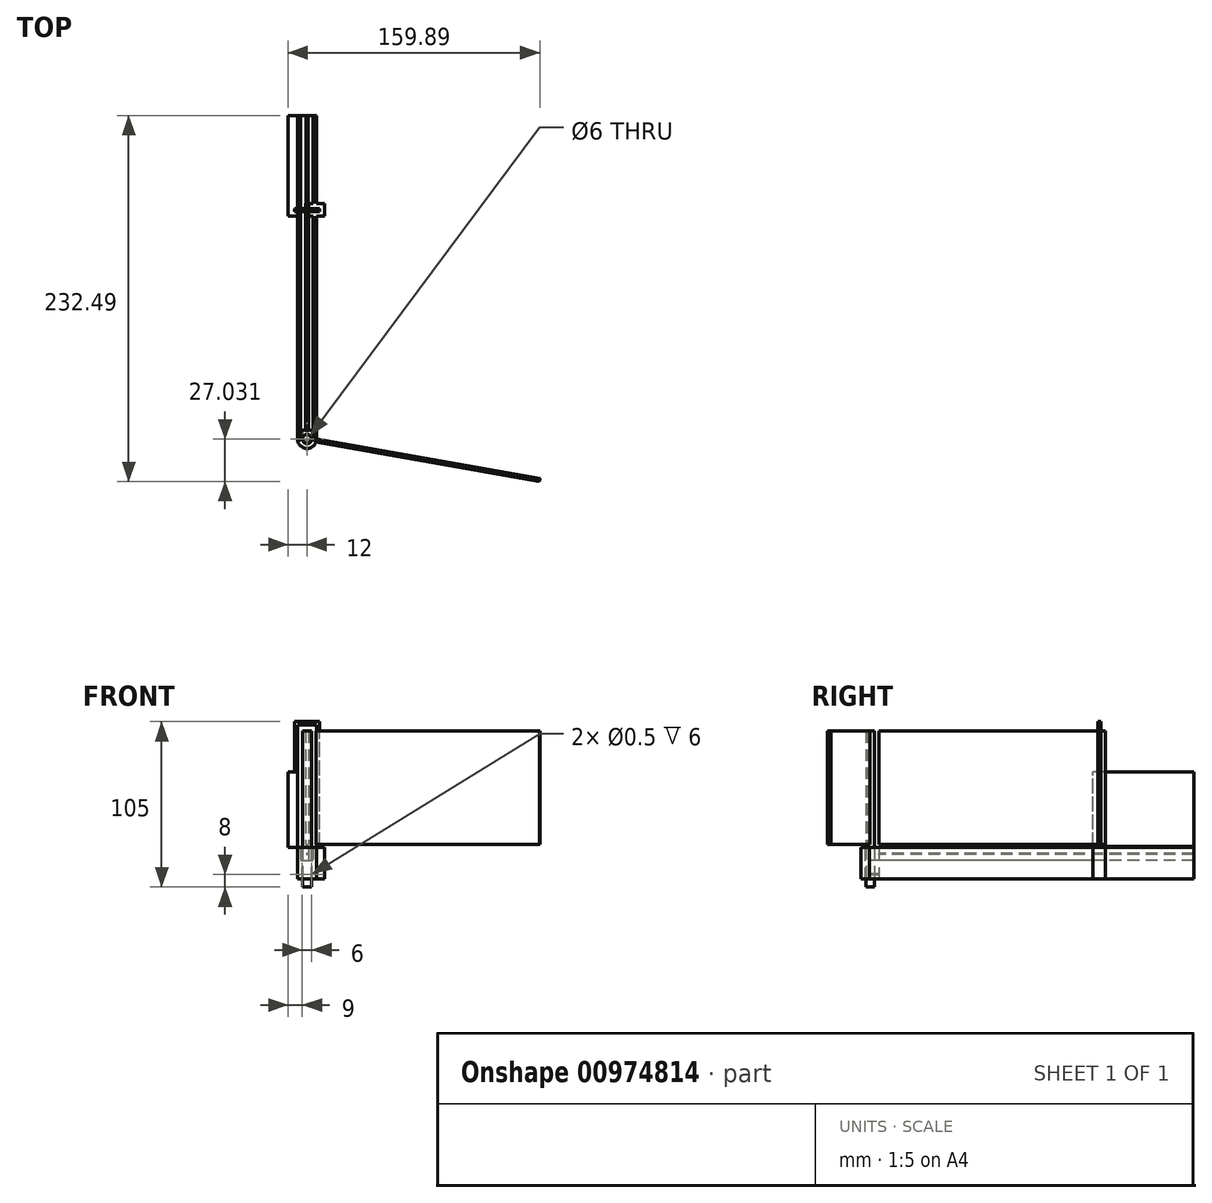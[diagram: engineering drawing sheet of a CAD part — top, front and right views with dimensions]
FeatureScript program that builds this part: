
annotation { "Feature Type Name" : "Feature", "Feature Type Description" : "" }
export const myFeature = defineFeature(function(context is Context, id is Id, definition is map)
    precondition{}
    {
        {
            var Q0;
            Q0=qCreatedBy(makeId("Front.planeOp"),FACE);
            var sketch = newSketch(context, id + "F0", { "sketchPlane" : qUnion([Q0])});
            skLineSegment(sketch, "E0.bottom", {"start": v(2, 0) * mm, "end": v(10, 0) * mm});
            skLineSegment(sketch, "E0.top", {"start": v(2, -8) * mm, "end": v(10, -8) * mm});
            skLineSegment(sketch, "E0.left", {"start": v(2, 0) * mm, "end": v(2, -8) * mm});
            skLineSegment(sketch, "E0.right", {"start": v(10, 0) * mm, "end": v(10, -8) * mm});
            skLineSegment(sketch, "E1.bottom", {"start": v(0, -8) * mm, "end": v(12, -8) * mm});
            skLineSegment(sketch, "E1.top", {"start": v(0, -20) * mm, "end": v(12, -20) * mm});
            skLineSegment(sketch, "E1.left", {"start": v(0, -8) * mm, "end": v(0, -20) * mm});
            skLineSegment(sketch, "E1.right", {"start": v(12, -8) * mm, "end": v(12, -20) * mm});
            skLineSegment(sketch, "E2.bottom", {"start": v(0, 0) * mm, "end": v(2, 0) * mm});
            skLineSegment(sketch, "E2.top", {"start": v(0, -8) * mm, "end": v(2, -8) * mm});
            skLineSegment(sketch, "E2.left", {"start": v(0, 0) * mm, "end": v(0, -8) * mm});
            skLineSegment(sketch, "E3.bottom", {"start": v(10, 0) * mm, "end": v(12, 0) * mm});
            skLineSegment(sketch, "E3.top", {"start": v(10, -8) * mm, "end": v(12, -8) * mm});
            skLineSegment(sketch, "E3.right", {"start": v(12, 0) * mm, "end": v(12, -8) * mm});
            skCircle(sketch, "E4", {"center": v(3, -17) * mm, "radius": 0.25 * mm});
            skCircle(sketch, "E5", {"center": v(9, -17) * mm, "radius": 0.25 * mm});
            skCircle(sketch, "E6", {"center": v(6, -4) * mm, "radius": 0.25 * mm});
            skLineSegment(sketch, "E7.bottom", {"start": v(4.5, 0) * mm, "end": v(7.5, 0) * mm});
            skLineSegment(sketch, "E7.top", {"start": v(4.5, 0.2) * mm, "end": v(7.5, 0.2) * mm});
            skLineSegment(sketch, "E7.left", {"start": v(4.5, 0) * mm, "end": v(4.5, 0.2) * mm});
            skLineSegment(sketch, "E7.right", {"start": v(7.5, 0) * mm, "end": v(7.5, 0.2) * mm});
            skLineSegment(sketch, "E8", {"start": v(5.59, 0.2) * mm, "end": v(6, 0.61) * mm});
            skLineSegment(sketch, "E9", {"start": v(6, 0.61) * mm, "end": v(6.41, 0.2) * mm});
            skLineSegment(sketch, "E10", {"start": v(6.41, 0.2) * mm, "end": v(6.53, 0.32) * mm});
            skLineSegment(sketch, "E11", {"start": v(6.53, 0.32) * mm, "end": v(6, 0.85) * mm});
            skLineSegment(sketch, "E12", {"start": v(6, 0.85) * mm, "end": v(5.47, 0.32) * mm});
            skLineSegment(sketch, "E13", {"start": v(5.47, 0.32) * mm, "end": v(5.59, 0.2) * mm});
            skSolve(sketch);
        }
        {
            var Q0;
            Q0=makeQuery(id+"F0.imprint","IMPRINT",FACE,{"disambiguationData":[TD([[makeQuery(id+"F0.imprint","IMPRINT",EDGE,{"derivedFrom":sQuery(id+"F0.wireOp",EDGE,"E1.bottom")}),1.0]])]});
            var Q1;
            Q1=makeQuery(id+"F0.imprint","IMPRINT",FACE,{"disambiguationData":[TD([[makeQuery(id+"F0.imprint","IMPRINT",EDGE,{"derivedFrom":sQuery(id+"F0.wireOp",EDGE,"E1.bottom")}),-1.0]])]});
            extrude(context, id + "F1", {"entities" : qUnion([Q0, Q1]), "oppositeDirection" : true, "depth" : 200 * mm, "offsetDistance" : 25 * mm, "hasSecondDirection" : true, "secondDirectionOppositeDirection" : false, "secondDirectionDepth" : 6 * mm});
        }
        {
            var Q0;
            Q0=makeQuery(id+"F0.imprint","IMPRINT",FACE,{"disambiguationData":[TD([[makeQuery(id+"F0.imprint","IMPRINT",EDGE,{"derivedFrom":sQuery(id+"F0.wireOp",EDGE,"E4")}),1.0]])]});
            var Q1;
            Q1=makeQuery(id+"F0.imprint","IMPRINT",FACE,{"disambiguationData":[TD([[makeQuery(id+"F0.imprint","IMPRINT",EDGE,{"derivedFrom":sQuery(id+"F0.wireOp",EDGE,"E5")}),1.0]])]});
            var Q2;
            Q2=makeQuery(id+"F0.imprint","IMPRINT",FACE,{"disambiguationData":[TD([[makeQuery(id+"F0.imprint","IMPRINT",EDGE,{"derivedFrom":sQuery(id+"F0.wireOp",EDGE,"E6")}),1.0]])]});
            var Q3;
            Q3=makeQuery(id+"F0.imprint","IMPRINT",FACE,{"disambiguationData":[TD([[makeQuery(id+"F0.imprint","IMPRINT",EDGE,{"derivedFrom":sQuery(id+"F0.wireOp",EDGE,"E7.bottom")}),1.0]])]});
            var Q4;
            Q4=makeQuery(id+"F0.imprint","IMPRINT",FACE,{"disambiguationData":[TD([[makeQuery(id+"F0.imprint","IMPRINT",EDGE,{"derivedFrom":sQuery(id+"F0.wireOp",EDGE,"E8")}),1.0]])]});
            extrude(context, id + "F2", {"entities" : qUnion([Q0, Q1, Q2, Q3, Q4]), "operationType" : NewBodyOperationType.ADD, "oppositeDirection" : true, "depth" : 200 * mm, "offsetDistance" : 25 * mm});
        }
        {
            var Q0;
            Q0=makeQuery(id+"F1.opExtrude","SWEPT_FACE",FACE,{"disambiguationData":[OSD([sQuery(id+"F0.wireOp",EDGE,"E1.right")])]});
            var sketch = newSketch(context, id + "F3", { "sketchPlane" : qUnion([Q0])});
            skLineSegment(sketch, "E14.bottom", {"start": v(136, 0) * mm, "end": v(144, 0) * mm});
            skLineSegment(sketch, "E14.top", {"start": v(136, -20) * mm, "end": v(144, -20) * mm});
            skLineSegment(sketch, "E14.left", {"start": v(136, 0) * mm, "end": v(136, -20) * mm});
            skLineSegment(sketch, "E14.right", {"start": v(144, 0) * mm, "end": v(144, -20) * mm});
            skSolve(sketch);
        }
        {
            var Q0;
            Q0 = qSketchRegion(id + "F3", true);
            extrude(context, id + "F4", {"entities" : qUnion([Q0]), "operationType" : NewBodyOperationType.ADD, "endBound" : BoundingType.SYMMETRIC, "depth" : 10 * mm, "offsetDistance" : 25 * mm});
        }
        {
            var Q0;
            Q0=qCreatedBy(makeId("Top.planeOp"),FACE);
            var sketch = newSketch(context, id + "F5", { "sketchPlane" : qUnion([Q0])});
            skCircle(sketch, "E15", {"center": v(6, -5.46) * mm, "radius": 3 * mm});
            skPoint(sketch, "E15.centerSnap0", {"position": v(6, 0) * mm});
            skCircle(sketch, "E16", {"center": v(6, -5.46) * mm, "radius": 6 * mm});
            skSolve(sketch);
        }
        {
            var Q0;
            Q0 = qSketchRegion(id + "F5", true);
            extrude(context, id + "F6", {"entities" : qUnion([Q0]), "oppositeDirection" : true, "depth" : 20 * mm, "offsetDistance" : 25 * mm});
        }
        {
            var Q0;
            Q0=makeQuery(id+"F4.opExtrude","SWEPT_FACE",FACE,{"disambiguationData":[OSD([sQuery(id+"F3.wireOp",EDGE,"E14.left")])]});
            var sketch = newSketch(context, id + "F7", { "sketchPlane" : qUnion([Q0])});
            skLineSegment(sketch, "E17.bottom", {"start": v(0, 0) * mm, "end": v(-6, 0) * mm});
            skLineSegment(sketch, "E17.top", {"start": v(0, 48) * mm, "end": v(-6, 48) * mm});
            skLineSegment(sketch, "E17.left", {"start": v(0, 0) * mm, "end": v(0, 48) * mm});
            skLineSegment(sketch, "E17.right", {"start": v(-6, 0) * mm, "end": v(-6, 48) * mm});
            skSolve(sketch);
        }
        {
            var Q0;
            Q0 = qSketchRegion(id + "F7", true);
            extrude(context, id + "F8", {"entities" : qUnion([Q0]), "oppositeDirection" : true, "depth" : 64 * mm, "offsetDistance" : 25 * mm});
        }
        {
            var Q0;
            Q0=makeQuery(id+"F8.opExtrude","CAP_FACE",FACE,{"disambiguationData":[OSD([sQuery(id+"F7.wireOp",EDGE,"E17.bottom"),sQuery(id+"F7.wireOp",EDGE,"E17.top"),sQuery(id+"F7.wireOp",EDGE,"E17.left"),sQuery(id+"F7.wireOp",EDGE,"E17.right")])],"isStart":true});
            var sketch = newSketch(context, id + "F9", { "sketchPlane" : qUnion([Q0])});
            skLineSegment(sketch, "E18", {"start": v(0, 48) * mm, "end": v(0, 78) * mm});
            skLineSegment(sketch, "E19", {"start": v(0, 78) * mm, "end": v(12, 78) * mm});
            skLineSegment(sketch, "E20", {"start": v(12, 78) * mm, "end": v(12, 0) * mm});
            skLineSegment(sketch, "E21", {"start": v(12, 0) * mm, "end": v(14, 0) * mm});
            skLineSegment(sketch, "E22", {"start": v(14, 0) * mm, "end": v(14, 80) * mm});
            skLineSegment(sketch, "E23", {"start": v(14, 80) * mm, "end": v(-2, 80) * mm});
            skLineSegment(sketch, "E24", {"start": v(-2, 80) * mm, "end": v(-2, 48) * mm});
            skLineSegment(sketch, "E25", {"start": v(-2, 48) * mm, "end": v(0, 48) * mm});
            skSolve(sketch);
        }
        {
            var Q0;
            Q0 = qSketchRegion(id + "F9", true);
            extrude(context, id + "F10", {"entities" : qUnion([Q0]), "oppositeDirection" : true, "depth" : 5 * mm, "offsetDistance" : 25 * mm, "hasSecondDirection" : true, "secondDirectionOppositeDirection" : false, "secondDirectionDepth" : -3 * mm});
        }
        {
            var Q0;
            Q0=qCreatedBy(makeId("Front.planeOp"),FACE);
            var sketch = newSketch(context, id + "F11", { "sketchPlane" : qUnion([Q0])});
            skLineSegment(sketch, "E26.bottom", {"start": v(5, 74) * mm, "end": v(7, 74) * mm});
            skLineSegment(sketch, "E26.top", {"start": v(5, 2) * mm, "end": v(7, 2) * mm});
            skLineSegment(sketch, "E26.left", {"start": v(5, 74) * mm, "end": v(5, 2) * mm});
            skLineSegment(sketch, "E26.right", {"start": v(7, 74) * mm, "end": v(7, 2) * mm});
            skSolve(sketch);
        }
        {
            var Q0;
            Q0 = qSketchRegion(id + "F11", true);
            extrude(context, id + "F12", {"entities" : qUnion([Q0]), "oppositeDirection" : true, "depth" : 144 * mm, "offsetDistance" : 25 * mm});
        }
        {
            var Q0;
            Q0=qCreatedBy(makeId("Top.planeOp"),FACE);
            var sketch = newSketch(context, id + "F13", { "sketchPlane" : qUnion([Q0])});
            skLineSegment(sketch, "E27.bottom", {"start": v(12.08, -5.52) * mm, "end": v(153.9, -30.52) * mm});
            skLineSegment(sketch, "E27.top", {"start": v(11.74, -7.49) * mm, "end": v(153.55, -32.5) * mm});
            skLineSegment(sketch, "E27.left", {"start": v(12.08, -5.52) * mm, "end": v(11.74, -7.49) * mm});
            skLineSegment(sketch, "E27.right", {"start": v(153.9, -30.52) * mm, "end": v(153.55, -32.5) * mm});
            skSolve(sketch);
        }
        {
            var Q0;
            Q0 = qSketchRegion(id + "F13", true);
            extrude(context, id + "F14", {"entities" : qUnion([Q0]), "depth" : 74 * mm, "offsetDistance" : 25 * mm, "hasSecondDirection" : true, "secondDirectionOppositeDirection" : false, "secondDirectionDepth" : 2 * mm});
        }
        {
            var Q0;
            Q0=qCreatedBy(makeId("Top.planeOp"),FACE);
            var sketch = newSketch(context, id + "F15", { "sketchPlane" : qUnion([Q0])});
            skCircle(sketch, "E28", {"center": v(6, -5.46) * mm, "radius": 2.75 * mm});
            skSolve(sketch);
        }
        {
            var Q0;
            Q0 = qSketchRegion(id + "F15", true);
            extrude(context, id + "F16", {"entities" : qUnion([Q0]), "depth" : 74 * mm, "offsetDistance" : 25 * mm, "hasSecondDirection" : true, "secondDirectionOppositeDirection" : true, "secondDirectionDepth" : 25 * mm});
        }
    });
